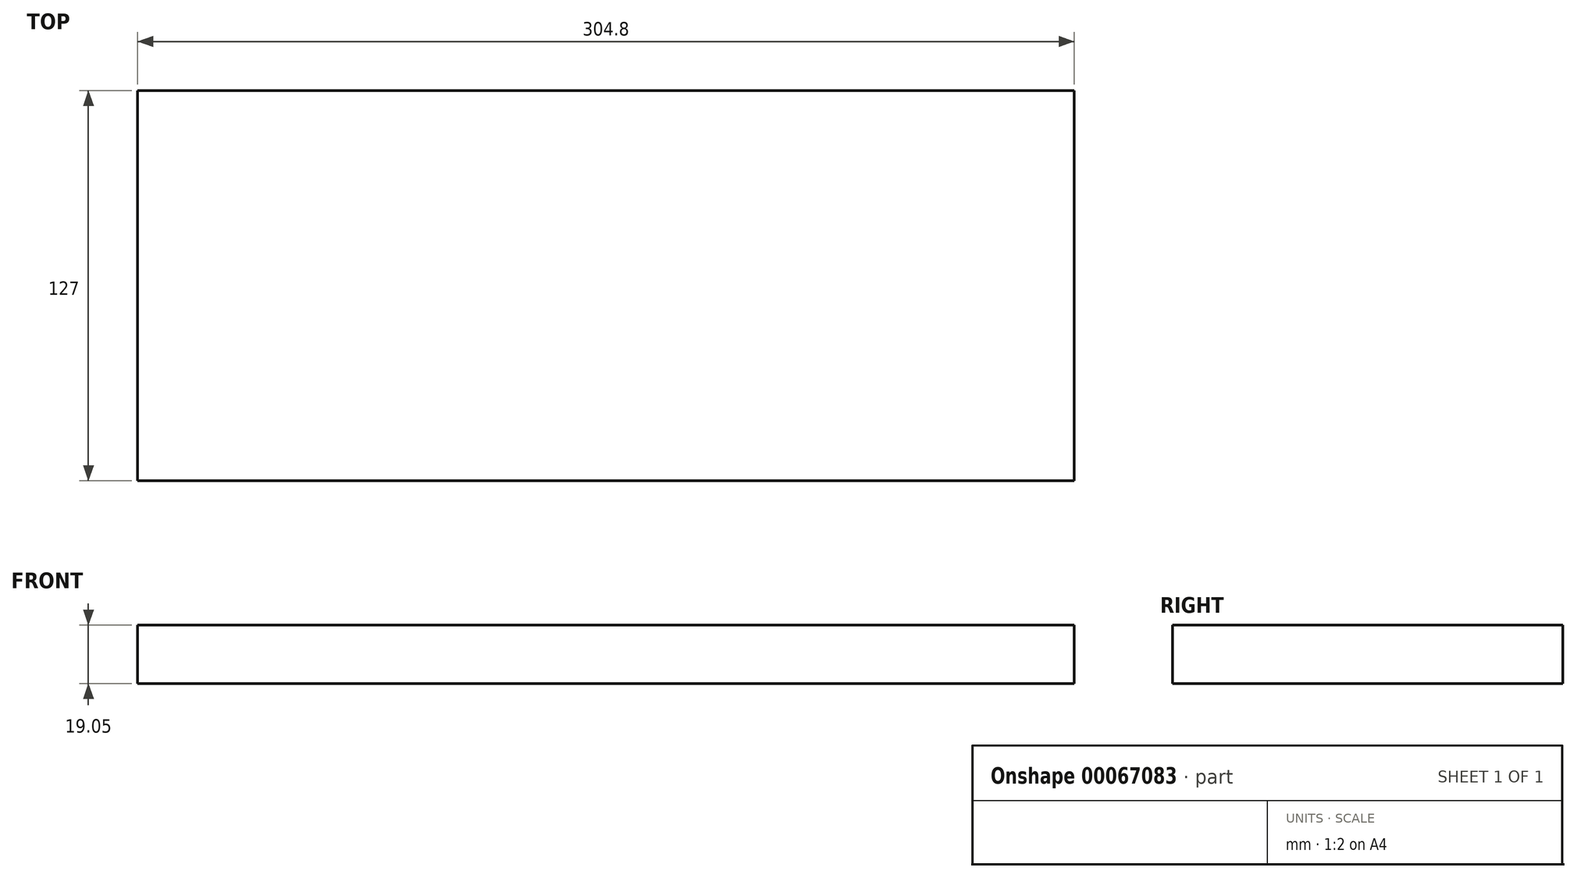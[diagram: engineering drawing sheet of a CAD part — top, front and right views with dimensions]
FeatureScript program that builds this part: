
annotation { "Feature Type Name" : "Feature", "Feature Type Description" : "" }
export const myFeature = defineFeature(function(context is Context, id is Id, definition is map)
    precondition{}
    {
        {
            var Q0;
            Q0=qCreatedBy(makeId("Top.planeOp"),FACE);
            var sketch = newSketch(context, id + "F0", { "sketchPlane" : qUnion([Q0])});
            skLineSegment(sketch, "E0.bottom", {"start": v(0, 0) * mm, "end": v(304.8, 0) * mm});
            skLineSegment(sketch, "E0.top", {"start": v(0, 127) * mm, "end": v(304.8, 127) * mm});
            skLineSegment(sketch, "E0.left", {"start": v(0, 0) * mm, "end": v(0, 127) * mm});
            skLineSegment(sketch, "E0.right", {"start": v(304.8, 0) * mm, "end": v(304.8, 127) * mm});
            skSolve(sketch);
        }
        {
            var Q0;
            Q0 = qSketchRegion(id + "F0", true);
            extrude(context, id + "F1", {"entities" : qUnion([Q0]), "depth" : 19.05 * mm});
        }
    });
